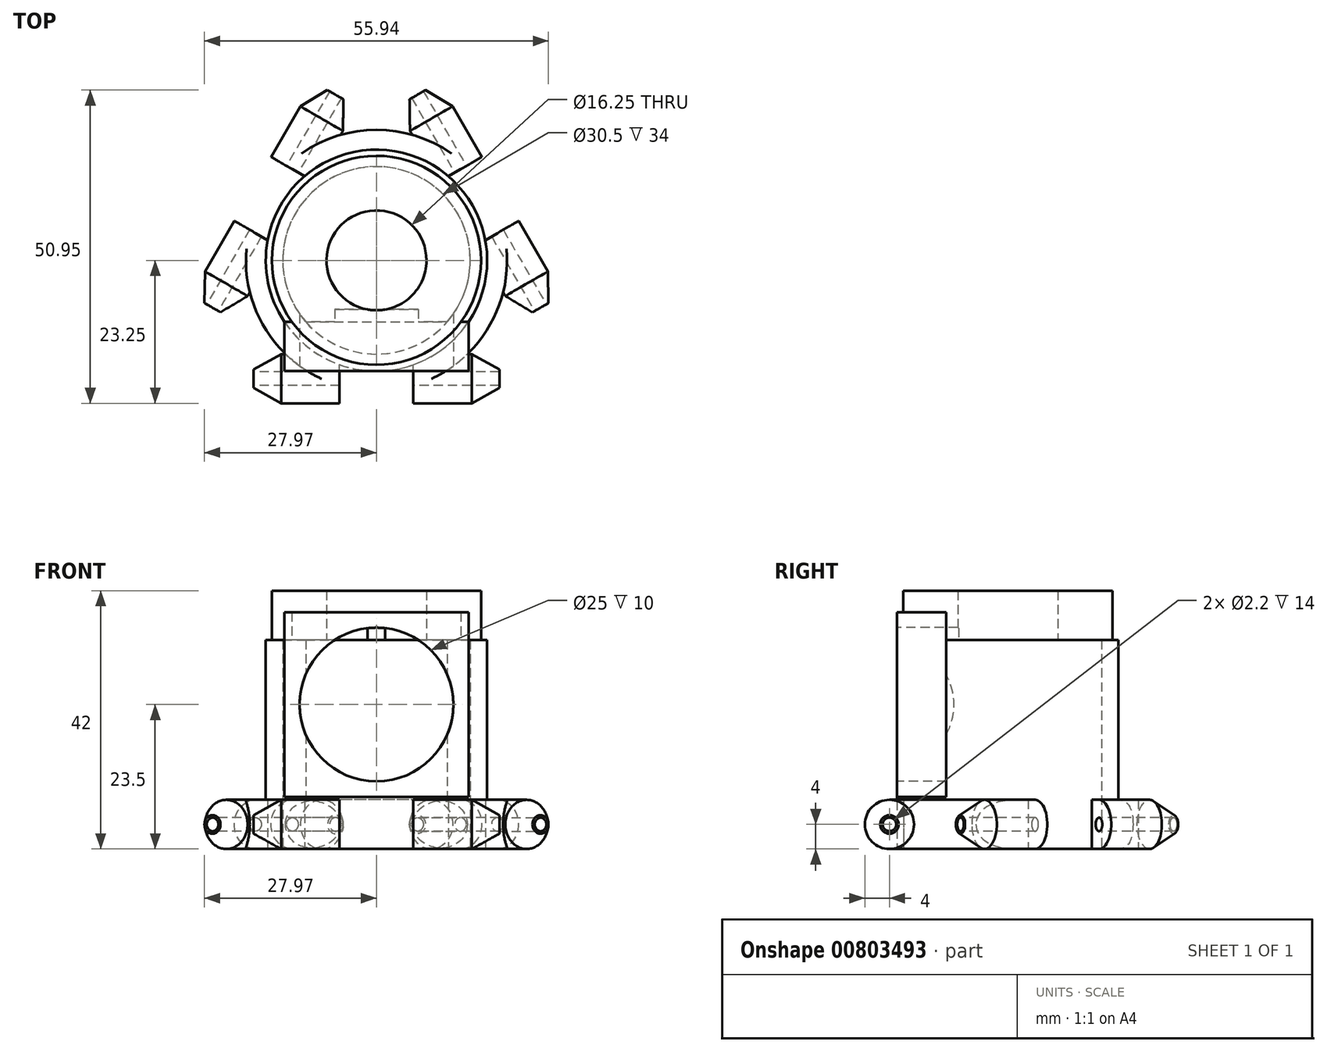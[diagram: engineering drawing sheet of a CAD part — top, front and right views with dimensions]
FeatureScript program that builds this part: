
annotation { "Feature Type Name" : "Feature", "Feature Type Description" : "" }
export const myFeature = defineFeature(function(context is Context, id is Id, definition is map)
    precondition{}
    {
        {
            var Q0;
            Q0=qCreatedBy(makeId("Top.planeOp"),FACE);
            var sketch = newSketch(context, id + "F0", { "sketchPlane" : qUnion([Q0])});
            skCircle(sketch, "E0", {"center": v(0, 0) * mm, "radius": 15.25 * mm});
            skLineSegment(sketch, "E1", {"start": v(0, 22.62) * mm, "end": v(0, -24.73) * mm, "construction": true});
            skLineSegment(sketch, "E2", {"start": v(0, 0) * mm, "end": v(23.85, 13.77) * mm, "construction": true});
            skLineSegment(sketch, "E3", {"start": v(0, 0) * mm, "end": v(-21.58, 12.46) * mm, "construction": true});
            skArc(sketch, "E4", {"start": v(-6, -16.97) * mm, "mid": v(0, -18) * mm, "end": v(6, -16.97) * mm});
            skLineSegment(sketch, "E5", {"start": v(0, -15.25) * mm, "end": v(-9.56, -15.25) * mm, "construction": true});
            skLineSegment(sketch, "E6", {"start": v(-14.78, -15.25) * mm, "end": v(-20, -15.25) * mm});
            skLineSegment(sketch, "E7", {"start": v(-20, -15.25) * mm, "end": v(-20, -23.25) * mm});
            skLineSegment(sketch, "E8", {"start": v(-20, -23.25) * mm, "end": v(-6, -23.25) * mm});
            skLineSegment(sketch, "E9", {"start": v(-6, -23.25) * mm, "end": v(-6, -16.97) * mm});
            skLineSegment(sketch, "E10.1.0", {"start": v(20.6, -5.18) * mm, "end": v(23.2, -9.7) * mm});
            skLineSegment(sketch, "E10.1.1", {"start": v(23.2, -9.7) * mm, "end": v(30.14, -5.7) * mm});
            skLineSegment(sketch, "E10.1.2", {"start": v(30.14, -5.7) * mm, "end": v(23.14, 6.43) * mm});
            skLineSegment(sketch, "E10.1.3", {"start": v(23.14, 6.43) * mm, "end": v(17.7, 3.29) * mm});
            skLineSegment(sketch, "E10.2.0", {"start": v(-5.82, 20.43) * mm, "end": v(-3.2, 24.95) * mm});
            skLineSegment(sketch, "E10.2.1", {"start": v(-3.2, 24.95) * mm, "end": v(-10.14, 28.95) * mm});
            skLineSegment(sketch, "E10.2.2", {"start": v(-10.14, 28.95) * mm, "end": v(-17.14, 16.82) * mm});
            skLineSegment(sketch, "E10.2.3", {"start": v(-17.14, 16.82) * mm, "end": v(-11.7, 13.68) * mm});
            skLineSegment(sketch, "E11.MirrorCS", {"start": v(17.14, 16.82) * mm, "end": v(11.7, 13.68) * mm});
            skLineSegment(sketch, "E12.MirrorCS", {"start": v(10.14, 28.95) * mm, "end": v(17.14, 16.82) * mm});
            skLineSegment(sketch, "E13.MirrorCS", {"start": v(3.2, 24.95) * mm, "end": v(10.14, 28.95) * mm});
            skLineSegment(sketch, "E14.MirrorCS", {"start": v(5.82, 20.43) * mm, "end": v(3.2, 24.95) * mm});
            skLineSegment(sketch, "E15.1.0", {"start": v(-23.14, 6.43) * mm, "end": v(-17.7, 3.29) * mm});
            skLineSegment(sketch, "E15.1.1", {"start": v(-30.14, -5.7) * mm, "end": v(-23.14, 6.43) * mm});
            skLineSegment(sketch, "E15.1.2", {"start": v(-23.2, -9.7) * mm, "end": v(-30.14, -5.7) * mm});
            skLineSegment(sketch, "E15.1.3", {"start": v(-20.6, -5.18) * mm, "end": v(-23.2, -9.7) * mm});
            skLineSegment(sketch, "E15.2.0", {"start": v(6, -23.25) * mm, "end": v(6, -16.97) * mm});
            skLineSegment(sketch, "E15.2.1", {"start": v(20, -23.25) * mm, "end": v(6, -23.25) * mm});
            skLineSegment(sketch, "E15.2.2", {"start": v(20, -15.25) * mm, "end": v(20, -23.25) * mm});
            skLineSegment(sketch, "E15.2.3", {"start": v(14.78, -15.25) * mm, "end": v(20, -15.25) * mm});
            skArc(sketch, "E16.trimOffspring", {"start": v(-11.7, 13.68) * mm, "mid": v(-15.59, 9) * mm, "end": v(-17.7, 3.29) * mm});
            skArc(sketch, "E17.trimOffspring", {"start": v(17.7, 3.29) * mm, "mid": v(15.59, 9) * mm, "end": v(11.7, 13.68) * mm});
            skArc(sketch, "E18", {"start": v(5.82, 20.43) * mm, "mid": v(0, 21.24) * mm, "end": v(-5.82, 20.43) * mm});
            skArc(sketch, "E19.1.0", {"start": v(-20.6, -5.18) * mm, "mid": v(-18.4, -10.62) * mm, "end": v(-14.78, -15.25) * mm});
            skArc(sketch, "E19.2.0", {"start": v(14.78, -15.25) * mm, "mid": v(18.4, -10.62) * mm, "end": v(20.6, -5.18) * mm});
            skPoint(sketch, "E20.orphan", {"position": v(-8.43, 15.9) * mm});
            skPoint(sketch, "E21.orphan", {"position": v(8.43, 15.9) * mm});
            skPoint(sketch, "E22.trimOffspring.end.orphan", {"position": v(17.99, -0.66) * mm});
            skPoint(sketch, "E23.orphan", {"position": v(9.56, -15.25) * mm});
            skPoint(sketch, "E24.orphan", {"position": v(-17.99, -0.66) * mm});
            skSolve(sketch);
        }
        {
            var Q0;
            Q0 = qSketchRegion(id + "F0", true);
            extrude(context, id + "F1", {"entities" : qUnion([Q0]), "depth" : 8 * mm, "offsetDistance" : 25 * mm});
        }
        {
            var Q0;
            Q0=makeQuery(id+"F1.opExtrude","CAP_EDGE",EDGE,{"disambiguationData":[OSD([sQuery(id+"F0.wireOp",EDGE,"E12.MirrorCS")])],"isStart":false});
            var Q1;
            Q1=makeQuery(id+"F1.opExtrude","CAP_EDGE",EDGE,{"disambiguationData":[OSD([sQuery(id+"F0.wireOp",EDGE,"E10.1.2")])],"isStart":false});
            var Q2;
            Q2=makeQuery(id+"F1.opExtrude","CAP_EDGE",EDGE,{"disambiguationData":[OSD([sQuery(id+"F0.wireOp",EDGE,"E15.2.1")])],"isStart":false});
            var Q3;
            Q3=makeQuery(id+"F1.opExtrude","CAP_EDGE",EDGE,{"disambiguationData":[OSD([sQuery(id+"F0.wireOp",EDGE,"E8")])],"isStart":false});
            var Q4;
            Q4=makeQuery(id+"F1.opExtrude","CAP_EDGE",EDGE,{"disambiguationData":[OSD([sQuery(id+"F0.wireOp",EDGE,"E15.1.1")])],"isStart":false});
            var Q5;
            Q5=makeQuery(id+"F1.opExtrude","CAP_EDGE",EDGE,{"disambiguationData":[OSD([sQuery(id+"F0.wireOp",EDGE,"E10.2.2")])],"isStart":false});
            var Q6;
            Q6=makeQuery(id+"F1.opExtrude","CAP_EDGE",EDGE,{"disambiguationData":[OSD([sQuery(id+"F0.wireOp",EDGE,"E10.2.0")])],"isStart":false});
            var Q7;
            Q7=makeQuery(id+"F1.opExtrude","CAP_EDGE",EDGE,{"disambiguationData":[OSD([sQuery(id+"F0.wireOp",EDGE,"E14.MirrorCS")])],"isStart":false});
            var Q8;
            Q8=makeQuery(id+"F1.opExtrude","CAP_EDGE",EDGE,{"disambiguationData":[OSD([sQuery(id+"F0.wireOp",EDGE,"E10.1.0")])],"isStart":false});
            var Q9;
            Q9=makeQuery(id+"F1.opExtrude","CAP_EDGE",EDGE,{"disambiguationData":[OSD([sQuery(id+"F0.wireOp",EDGE,"E15.2.3")])],"isStart":false});
            var Q10;
            Q10=makeQuery(id+"F1.opExtrude","CAP_EDGE",EDGE,{"disambiguationData":[OSD([sQuery(id+"F0.wireOp",EDGE,"E6")])],"isStart":false});
            var Q11;
            Q11=makeQuery(id+"F1.opExtrude","CAP_EDGE",EDGE,{"disambiguationData":[OSD([sQuery(id+"F0.wireOp",EDGE,"E15.1.3")])],"isStart":false});
            var Q12;
            Q12=makeQuery(id+"F1.opExtrude","CAP_EDGE",EDGE,{"disambiguationData":[OSD([sQuery(id+"F0.wireOp",EDGE,"E10.2.2")])],"isStart":true});
            var Q13;
            Q13=makeQuery(id+"F1.opExtrude","CAP_EDGE",EDGE,{"disambiguationData":[OSD([sQuery(id+"F0.wireOp",EDGE,"E15.1.1")])],"isStart":true});
            var Q14;
            Q14=makeQuery(id+"F1.opExtrude","CAP_EDGE",EDGE,{"disambiguationData":[OSD([sQuery(id+"F0.wireOp",EDGE,"E8")])],"isStart":true});
            var Q15;
            Q15=makeQuery(id+"F1.opExtrude","CAP_EDGE",EDGE,{"disambiguationData":[OSD([sQuery(id+"F0.wireOp",EDGE,"E15.2.1")])],"isStart":true});
            var Q16;
            Q16=makeQuery(id+"F1.opExtrude","CAP_EDGE",EDGE,{"disambiguationData":[OSD([sQuery(id+"F0.wireOp",EDGE,"E10.1.2")])],"isStart":true});
            var Q17;
            Q17=makeQuery(id+"F1.opExtrude","CAP_EDGE",EDGE,{"disambiguationData":[OSD([sQuery(id+"F0.wireOp",EDGE,"E12.MirrorCS")])],"isStart":true});
            var Q18;
            Q18=makeQuery(id+"F1.opExtrude","CAP_EDGE",EDGE,{"disambiguationData":[OSD([sQuery(id+"F0.wireOp",EDGE,"E14.MirrorCS")])],"isStart":true});
            var Q19;
            Q19=makeQuery(id+"F1.opExtrude","CAP_EDGE",EDGE,{"disambiguationData":[OSD([sQuery(id+"F0.wireOp",EDGE,"E10.2.0")])],"isStart":true});
            var Q20;
            Q20=makeQuery(id+"F1.opExtrude","CAP_EDGE",EDGE,{"disambiguationData":[OSD([sQuery(id+"F0.wireOp",EDGE,"E15.1.3")])],"isStart":true});
            var Q21;
            Q21=makeQuery(id+"F1.opExtrude","CAP_EDGE",EDGE,{"disambiguationData":[OSD([sQuery(id+"F0.wireOp",EDGE,"E6")])],"isStart":true});
            var Q22;
            Q22=makeQuery(id+"F1.opExtrude","CAP_EDGE",EDGE,{"disambiguationData":[OSD([sQuery(id+"F0.wireOp",EDGE,"E15.2.3")])],"isStart":true});
            var Q23;
            Q23=makeQuery(id+"F1.opExtrude","CAP_EDGE",EDGE,{"disambiguationData":[OSD([sQuery(id+"F0.wireOp",EDGE,"E10.1.0")])],"isStart":true});
            fillet(context, id + "F2", {"entities" : qUnion([Q0, Q1, Q2, Q3, Q4, Q5, Q6, Q7, Q8, Q9, Q10, Q11, Q12, Q13, Q14, Q15, Q16, Q17, Q18, Q19, Q20, Q21, Q22, Q23]), "tangentPropagation" : true, "radius" : 4 * mm, "defaultsChanged" : false, "vertexSettings" : [], "allowEdgeOverflow" : false});
        }
        {
            var Q0;
            Q0=makeQuery(id+"F2.opFillet","BLEND_EDGE",EDGE,{"blendedFrom":[makeQuery(id+"F1.opExtrude","CAP_EDGE",EDGE,{"disambiguationData":[OSD([sQuery(id+"F0.wireOp",EDGE,"E15.1.1")])],"isStart":true}),makeQuery(id+"F1.opExtrude","SWEPT_FACE",FACE,{"disambiguationData":[OSD([sQuery(id+"F0.wireOp",EDGE,"E15.1.2")])]})],"blendedInto":[makeQuery(id+"F1.opExtrude","SWEPT_FACE",FACE,{"disambiguationData":[OSD([sQuery(id+"F0.wireOp",EDGE,"E15.1.2")])]})]});
            var Q1;
            Q1=makeQuery(id+"F2.opFillet","BLEND_EDGE",EDGE,{"blendedFrom":[makeQuery(id+"F1.opExtrude","CAP_EDGE",EDGE,{"disambiguationData":[OSD([sQuery(id+"F0.wireOp",EDGE,"E12.MirrorCS")])],"isStart":true}),makeQuery(id+"F1.opExtrude","SWEPT_FACE",FACE,{"disambiguationData":[OSD([sQuery(id+"F0.wireOp",EDGE,"E13.MirrorCS")])]})],"blendedInto":[makeQuery(id+"F1.opExtrude","SWEPT_FACE",FACE,{"disambiguationData":[OSD([sQuery(id+"F0.wireOp",EDGE,"E13.MirrorCS")])]})]});
            var Q2;
            Q2=makeQuery(id+"F2.opFillet","BLEND_EDGE",EDGE,{"blendedFrom":[makeQuery(id+"F1.opExtrude","CAP_EDGE",EDGE,{"disambiguationData":[OSD([sQuery(id+"F0.wireOp",EDGE,"E10.1.0")])],"isStart":true}),makeQuery(id+"F1.opExtrude","SWEPT_FACE",FACE,{"disambiguationData":[OSD([sQuery(id+"F0.wireOp",EDGE,"E10.1.1")])]})],"blendedInto":[makeQuery(id+"F1.opExtrude","SWEPT_FACE",FACE,{"disambiguationData":[OSD([sQuery(id+"F0.wireOp",EDGE,"E10.1.1")])]})]});
            var Q3;
            Q3=makeQuery(id+"F2.opFillet","BLEND_EDGE",EDGE,{"blendedFrom":[makeQuery(id+"F1.opExtrude","CAP_EDGE",EDGE,{"disambiguationData":[OSD([sQuery(id+"F0.wireOp",EDGE,"E15.2.1")])],"isStart":true}),makeQuery(id+"F1.opExtrude","SWEPT_FACE",FACE,{"disambiguationData":[OSD([sQuery(id+"F0.wireOp",EDGE,"E15.2.2")])]})],"blendedInto":[makeQuery(id+"F1.opExtrude","SWEPT_FACE",FACE,{"disambiguationData":[OSD([sQuery(id+"F0.wireOp",EDGE,"E15.2.2")])]})]});
            var Q4;
            Q4=makeQuery(id+"F2.opFillet","BLEND_EDGE",EDGE,{"blendedFrom":[makeQuery(id+"F1.opExtrude","CAP_EDGE",EDGE,{"disambiguationData":[OSD([sQuery(id+"F0.wireOp",EDGE,"E6")])],"isStart":true}),makeQuery(id+"F1.opExtrude","SWEPT_FACE",FACE,{"disambiguationData":[OSD([sQuery(id+"F0.wireOp",EDGE,"E7")])]})],"blendedInto":[makeQuery(id+"F1.opExtrude","SWEPT_FACE",FACE,{"disambiguationData":[OSD([sQuery(id+"F0.wireOp",EDGE,"E7")])]})]});
            var Q5;
            Q5=makeQuery(id+"F2.opFillet","BLEND_EDGE",EDGE,{"blendedFrom":[makeQuery(id+"F1.opExtrude","CAP_EDGE",EDGE,{"disambiguationData":[OSD([sQuery(id+"F0.wireOp",EDGE,"E10.2.0")])],"isStart":true}),makeQuery(id+"F1.opExtrude","SWEPT_FACE",FACE,{"disambiguationData":[OSD([sQuery(id+"F0.wireOp",EDGE,"E10.2.1")])]})],"blendedInto":[makeQuery(id+"F1.opExtrude","SWEPT_FACE",FACE,{"disambiguationData":[OSD([sQuery(id+"F0.wireOp",EDGE,"E10.2.1")])]})]});
            chamfer(context, id + "F3", {"entities" : qUnion([Q0, Q1, Q2, Q3, Q4, Q5]), "chamferType" : ChamferType.TWO_OFFSETS, "width1" : 2.5 * mm, "oppositeDirection" : false, "width2" : 4.5 * mm, "tangentPropagation" : true});
        }
        {
            var Q0;
            Q0=makeQuery(id+"F1.opExtrude","SWEPT_FACE",FACE,{"disambiguationData":[OSD([sQuery(id+"F0.wireOp",EDGE,"E15.1.2")])]});
            var sketch = newSketch(context, id + "F4", { "sketchPlane" : qUnion([Q0])});
            skCircle(sketch, "E25", {"center": v(-19.25, 4) * mm, "radius": 1.1 * mm});
            skSolve(sketch);
        }
        {
            var Q0;
            Q0 = qSketchRegion(id + "F4", true);
            extrude(context, id + "F5", {"entities" : qUnion([Q0]), "operationType" : NewBodyOperationType.REMOVE, "oppositeDirection" : true, "depth" : 41 * mm, "offsetDistance" : 25 * mm});
        }
        {
            var Q0;
            Q0=makeQuery(id+"F1.opExtrude","SWEPT_FACE",FACE,{"disambiguationData":[OSD([sQuery(id+"F0.wireOp",EDGE,"E7")])]});
            var sketch = newSketch(context, id + "F6", { "sketchPlane" : qUnion([Q0])});
            skCircle(sketch, "E26", {"center": v(19.25, 4) * mm, "radius": 1.1 * mm});
            skSolve(sketch);
        }
        {
            var Q0;
            Q0 = qSketchRegion(id + "F6", true);
            extrude(context, id + "F7", {"entities" : qUnion([Q0]), "operationType" : NewBodyOperationType.REMOVE, "oppositeDirection" : true, "depth" : 41 * mm, "offsetDistance" : 25 * mm});
        }
        {
            var Q0;
            Q0=makeQuery(id+"F1.opExtrude","SWEPT_FACE",FACE,{"disambiguationData":[OSD([sQuery(id+"F0.wireOp",EDGE,"E10.1.1")])]});
            var sketch = newSketch(context, id + "F8", { "sketchPlane" : qUnion([Q0])});
            skCircle(sketch, "E27", {"center": v(19.25, 4) * mm, "radius": 1.1 * mm});
            skSolve(sketch);
        }
        {
            var Q0;
            Q0 = qSketchRegion(id + "F8", true);
            extrude(context, id + "F9", {"entities" : qUnion([Q0]), "operationType" : NewBodyOperationType.REMOVE, "oppositeDirection" : true, "depth" : 41 * mm, "offsetDistance" : 25 * mm});
        }
        {
            var Q0;
            Q0=makeQuery(id+"F1.opExtrude","CAP_FACE",FACE,{"disambiguationData":[OSD([sQuery(id+"F0.wireOp",EDGE,"E0"),sQuery(id+"F0.wireOp",EDGE,"E4"),sQuery(id+"F0.wireOp",EDGE,"E6"),sQuery(id+"F0.wireOp",EDGE,"E7"),sQuery(id+"F0.wireOp",EDGE,"E8"),sQuery(id+"F0.wireOp",EDGE,"E9"),sQuery(id+"F0.wireOp",EDGE,"E10.1.0"),sQuery(id+"F0.wireOp",EDGE,"E10.1.1"),sQuery(id+"F0.wireOp",EDGE,"E10.1.2"),sQuery(id+"F0.wireOp",EDGE,"E10.1.3"),sQuery(id+"F0.wireOp",EDGE,"E10.2.0"),sQuery(id+"F0.wireOp",EDGE,"E10.2.1"),sQuery(id+"F0.wireOp",EDGE,"E10.2.2"),sQuery(id+"F0.wireOp",EDGE,"E10.2.3"),sQuery(id+"F0.wireOp",EDGE,"E11.MirrorCS"),sQuery(id+"F0.wireOp",EDGE,"E12.MirrorCS"),sQuery(id+"F0.wireOp",EDGE,"E13.MirrorCS"),sQuery(id+"F0.wireOp",EDGE,"E14.MirrorCS"),sQuery(id+"F0.wireOp",EDGE,"E15.1.0"),sQuery(id+"F0.wireOp",EDGE,"E15.1.1"),sQuery(id+"F0.wireOp",EDGE,"E15.1.2"),sQuery(id+"F0.wireOp",EDGE,"E15.1.3"),sQuery(id+"F0.wireOp",EDGE,"E15.2.0"),sQuery(id+"F0.wireOp",EDGE,"E15.2.1"),sQuery(id+"F0.wireOp",EDGE,"E15.2.2"),sQuery(id+"F0.wireOp",EDGE,"E15.2.3"),sQuery(id+"F0.wireOp",EDGE,"E16.trimOffspring"),sQuery(id+"F0.wireOp",EDGE,"E17.trimOffspring"),sQuery(id+"F0.wireOp",EDGE,"E18"),sQuery(id+"F0.wireOp",EDGE,"E19.1.0"),sQuery(id+"F0.wireOp",EDGE,"E19.2.0")])],"isStart":false});
            var sketch = newSketch(context, id + "F10", { "sketchPlane" : qUnion([Q0])});
            skCircle(sketch, "E28", {"center": v(0, 0) * mm, "radius": 15.25 * mm});
            skCircle(sketch, "E29", {"center": v(0, 0) * mm, "radius": 18 * mm});
            skSolve(sketch);
        }
        {
            var Q0;
            Q0=makeQuery(id+"F10.imprint","IMPRINT",FACE,{"disambiguationData":[TD([[makeQuery(id+"F10.imprint","IMPRINT",EDGE,{"derivedFrom":sQuery(id+"F10.wireOp",EDGE,"E28")}),-1.0]])]});
            extrude(context, id + "F11", {"entities" : qUnion([Q0]), "operationType" : NewBodyOperationType.ADD, "depth" : 26 * mm, "offsetDistance" : 25 * mm});
        }
        {
            var Q0;
            Q0=makeQuery(id+"F11.opExtrude","CAP_FACE",FACE,{"disambiguationData":[OSD([sQuery(id+"F10.wireOp",EDGE,"E28"),sQuery(id+"F10.wireOp",EDGE,"E29")])],"isStart":false});
            var sketch = newSketch(context, id + "F12", { "sketchPlane" : qUnion([Q0])});
            skCircle(sketch, "E30", {"center": v(0, 0) * mm, "radius": 8.12 * mm});
            skCircle(sketch, "E31", {"center": v(0, 0) * mm, "radius": 17 * mm});
            skSolve(sketch);
        }
        {
            var Q0;
            Q0 = qSketchRegion(id + "F12", true);
            extrude(context, id + "F13", {"entities" : qUnion([Q0]), "operationType" : NewBodyOperationType.ADD, "depth" : 8 * mm, "offsetDistance" : 25 * mm});
        }
        {
            var Q0;
            Q0=qCreatedBy(makeId("Front.planeOp"),FACE);
            var sketch = newSketch(context, id + "F14", { "sketchPlane" : qUnion([Q0])});
            skLineSegment(sketch, "E32", {"start": v(0, 49.23) * mm, "end": v(0, 0) * mm, "construction": true});
            skLineSegment(sketch, "E33.bottom", {"start": v(-15, 38.5) * mm, "end": v(15, 38.5) * mm});
            skLineSegment(sketch, "E33.top", {"start": v(-15, 8.5) * mm, "end": v(15, 8.5) * mm});
            skLineSegment(sketch, "E33.left", {"start": v(-15, 38.5) * mm, "end": v(-15, 8.5) * mm});
            skLineSegment(sketch, "E33.right", {"start": v(15, 38.5) * mm, "end": v(15, 8.5) * mm});
            skPoint(sketch, "E33.middle", {"position": v(0, 23.5) * mm});
            skSolve(sketch);
        }
        {
            var Q0;
            Q0 = qSketchRegion(id + "F14", true);
            extrude(context, id + "F15", {"entities" : qUnion([Q0]), "operationType" : NewBodyOperationType.ADD, "depth" : 18 * mm, "offsetDistance" : 25 * mm, "hasSecondDirection" : true, "secondDirectionOppositeDirection" : false, "secondDirectionDepth" : 10 * mm});
        }
        {
            var Q0;
            Q0=makeQuery(id+"F15.opExtrude","CAP_FACE",FACE,{"disambiguationData":[OSD([sQuery(id+"F14.wireOp",EDGE,"E33.bottom"),sQuery(id+"F14.wireOp",EDGE,"E33.top"),sQuery(id+"F14.wireOp",EDGE,"E33.left"),sQuery(id+"F14.wireOp",EDGE,"E33.right")])],"isStart":false});
            var sketch = newSketch(context, id + "F16", { "sketchPlane" : qUnion([Q0])});
            skCircle(sketch, "E34", {"center": v(0, 23.5) * mm, "radius": 12.5 * mm});
            skPoint(sketch, "E34.centerSnap0", {"position": v(-15, 23.5) * mm});
            skSolve(sketch);
        }
        {
            var Q0;
            Q0 = qSketchRegion(id + "F16", true);
            extrude(context, id + "F17", {"entities" : qUnion([Q0]), "operationType" : NewBodyOperationType.REMOVE, "oppositeDirection" : true, "depth" : 10 * mm, "offsetDistance" : 25 * mm});
        }
    });
